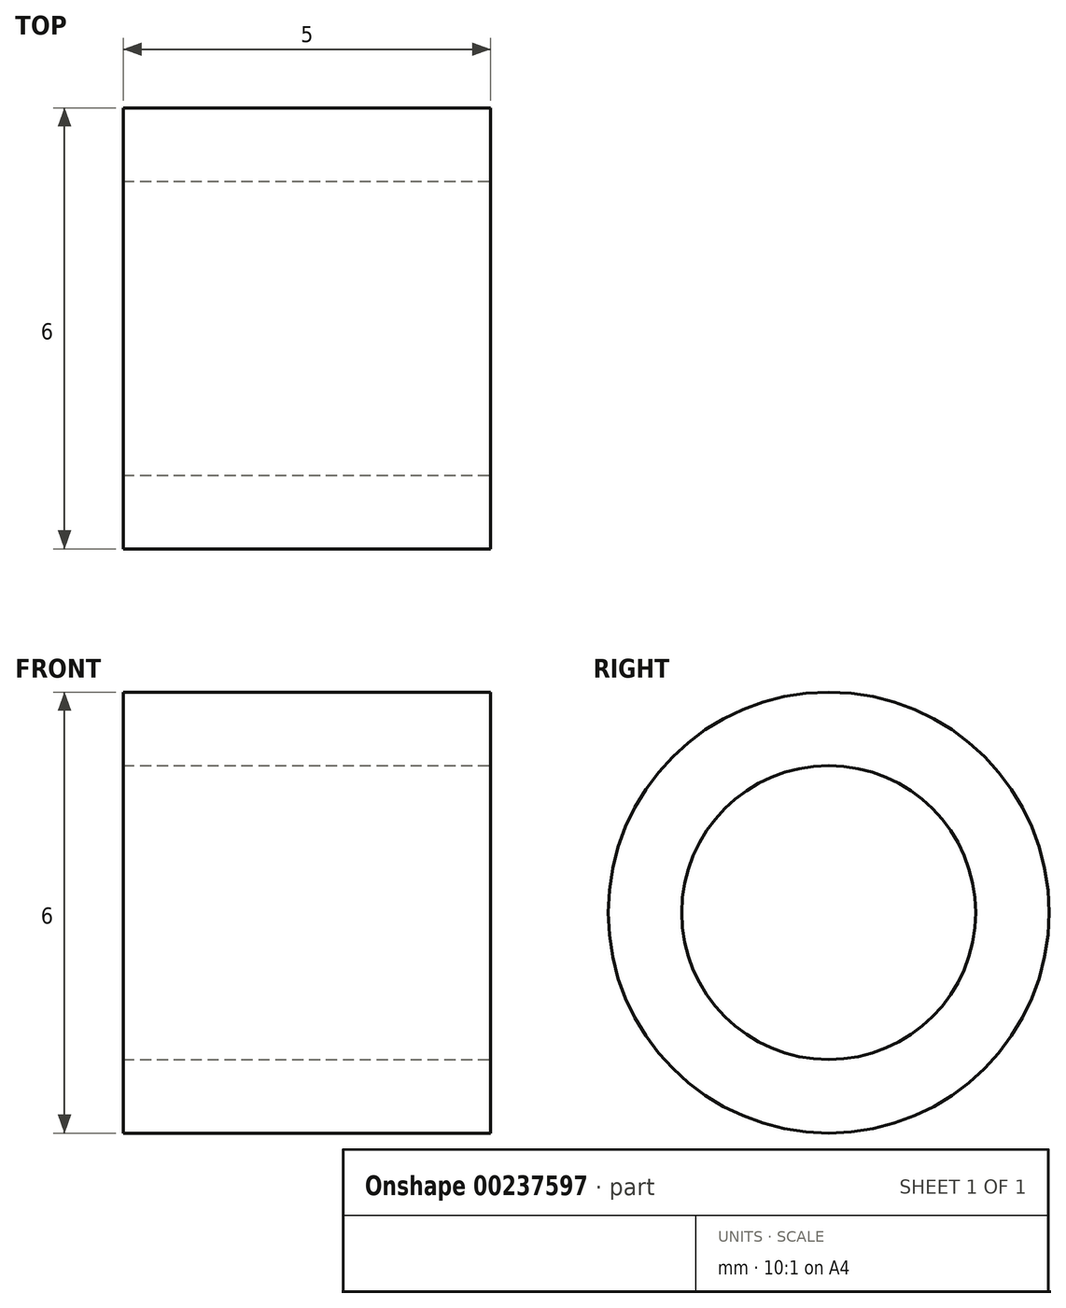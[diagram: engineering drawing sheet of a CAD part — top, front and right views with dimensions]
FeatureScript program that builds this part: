
annotation { "Feature Type Name" : "Feature", "Feature Type Description" : "" }
export const myFeature = defineFeature(function(context is Context, id is Id, definition is map)
    precondition{}
    {
        {
            var Q0;
            Q0=qCreatedBy(makeId("Right.planeOp"),FACE);
            var sketch = newSketch(context, id + "F0", { "sketchPlane" : qUnion([Q0])});
            skCircle(sketch, "E0", {"center": v(0, 0) * mm, "radius": 3 * mm});
            skSolve(sketch);
        }
        {
            var Q0;
            Q0 = qSketchRegion(id + "F0", true);
            extrude(context, id + "F1", {"entities" : qUnion([Q0]), "oppositeDirection" : true, "depth" : 5 * mm});
        }
        {
            var Q0;
            Q0=makeQuery(id+"F1.opExtrude","CAP_FACE",FACE,{"disambiguationData":[OSD([sQuery(id+"F0.wireOp",EDGE,"E0")])],"isStart":true});
            var Q1;
            Q1=makeQuery(id+"F1.opExtrude","CAP_FACE",FACE,{"disambiguationData":[OSD([sQuery(id+"F0.wireOp",EDGE,"E0")])],"isStart":false});
            shell(context, id + "F2", {"entities" : qUnion([Q0, Q1]), "thickness" : 1 * mm});
        }
    });
